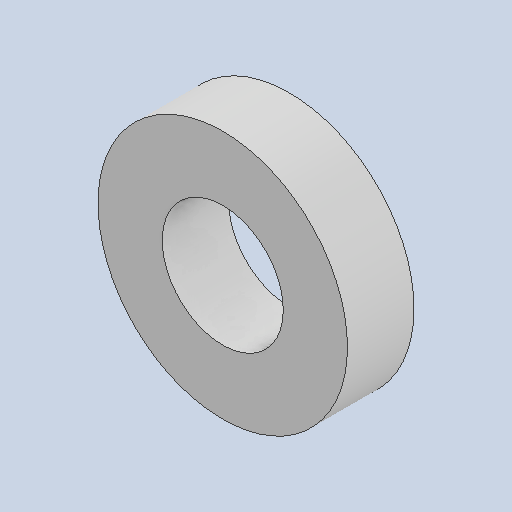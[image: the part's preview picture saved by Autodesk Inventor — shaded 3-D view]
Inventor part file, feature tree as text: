
AUTODESK INVENTOR PART (.ipt)
format: ipt  version: 2023 (Build 270158000, 158)  size: 94,720 bytes
history: native  units: in
note: dims shown in document units (in); Inventor stores cm internally (conversion verified against a paired STEP export)
features: other x3, sketch x1
ambient origin geometry x8: Origin, YZ Plane, XZ Plane, XY Plane, X Axis, Y Axis, Z Axis, Center Point
bodies: Solid1 (feature_tree)
feature tree (4):
  other  "100spacer.ipt"
  other  "Solid1::100spacer.ipt"
  other  "TaggingFeature1"
  sketch  "Sketch1"  dims[d0=0.3937in]
